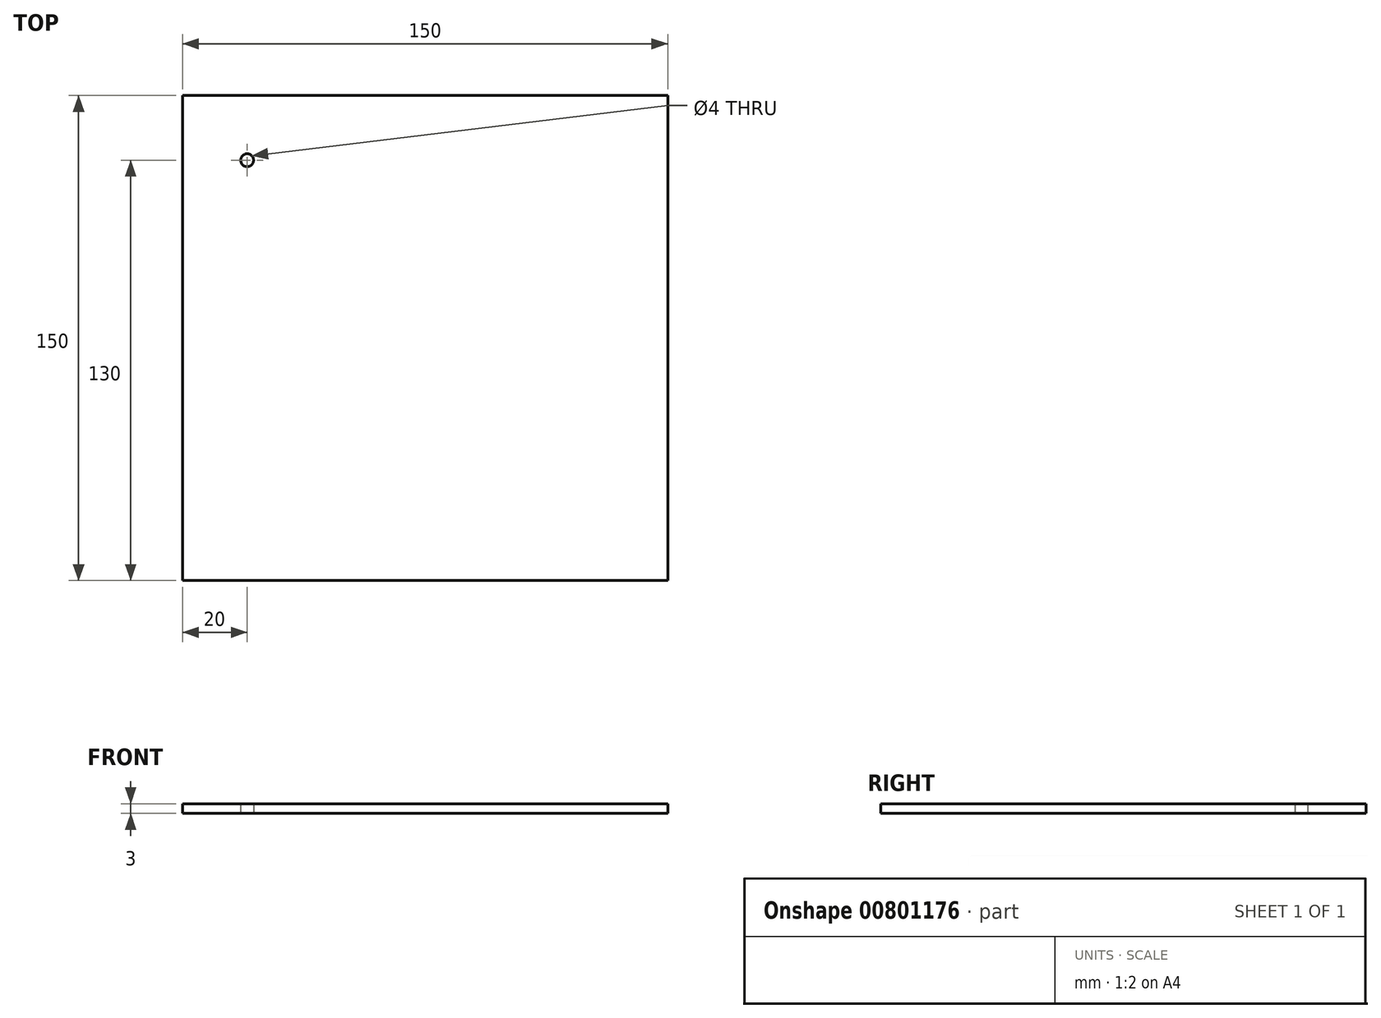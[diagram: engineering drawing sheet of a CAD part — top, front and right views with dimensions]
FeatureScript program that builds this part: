
annotation { "Feature Type Name" : "Feature", "Feature Type Description" : "" }
export const myFeature = defineFeature(function(context is Context, id is Id, definition is map)
    precondition{}
    {
        {
            var Q0;
            Q0=qCreatedBy(makeId("Top.planeOp"),FACE);
            var sketch = newSketch(context, id + "F0", { "sketchPlane" : qUnion([Q0])});
            skLineSegment(sketch, "E0.bottom", {"start": v(-75, 75) * mm, "end": v(75, 75) * mm});
            skLineSegment(sketch, "E0.top", {"start": v(-75, -75) * mm, "end": v(75, -75) * mm});
            skLineSegment(sketch, "E0.left", {"start": v(-75, 75) * mm, "end": v(-75, -75) * mm});
            skLineSegment(sketch, "E0.right", {"start": v(75, 75) * mm, "end": v(75, -75) * mm});
            skPoint(sketch, "E0.middle", {"position": v(0, 0) * mm});
            skCircle(sketch, "E1", {"center": v(-55, 55) * mm, "radius": 2 * mm});
            skSolve(sketch);
        }
        {
            var Q0;
            Q0=makeQuery(id+"F0.imprint","IMPRINT",FACE,{"disambiguationData":[TD([[makeQuery(id+"F0.imprint","IMPRINT",EDGE,{"derivedFrom":sQuery(id+"F0.wireOp",EDGE,"E0.bottom")}),-1.0]])]});
            extrude(context, id + "F1", {"entities" : qUnion([Q0]), "flatOperationType" : FlatOperationType.REMOVE, "depth" : 3 * mm, "offsetDistance" : 25 * mm, "domain" : OperationDomain.MODEL, "symmetric" : true});
        }
    });
